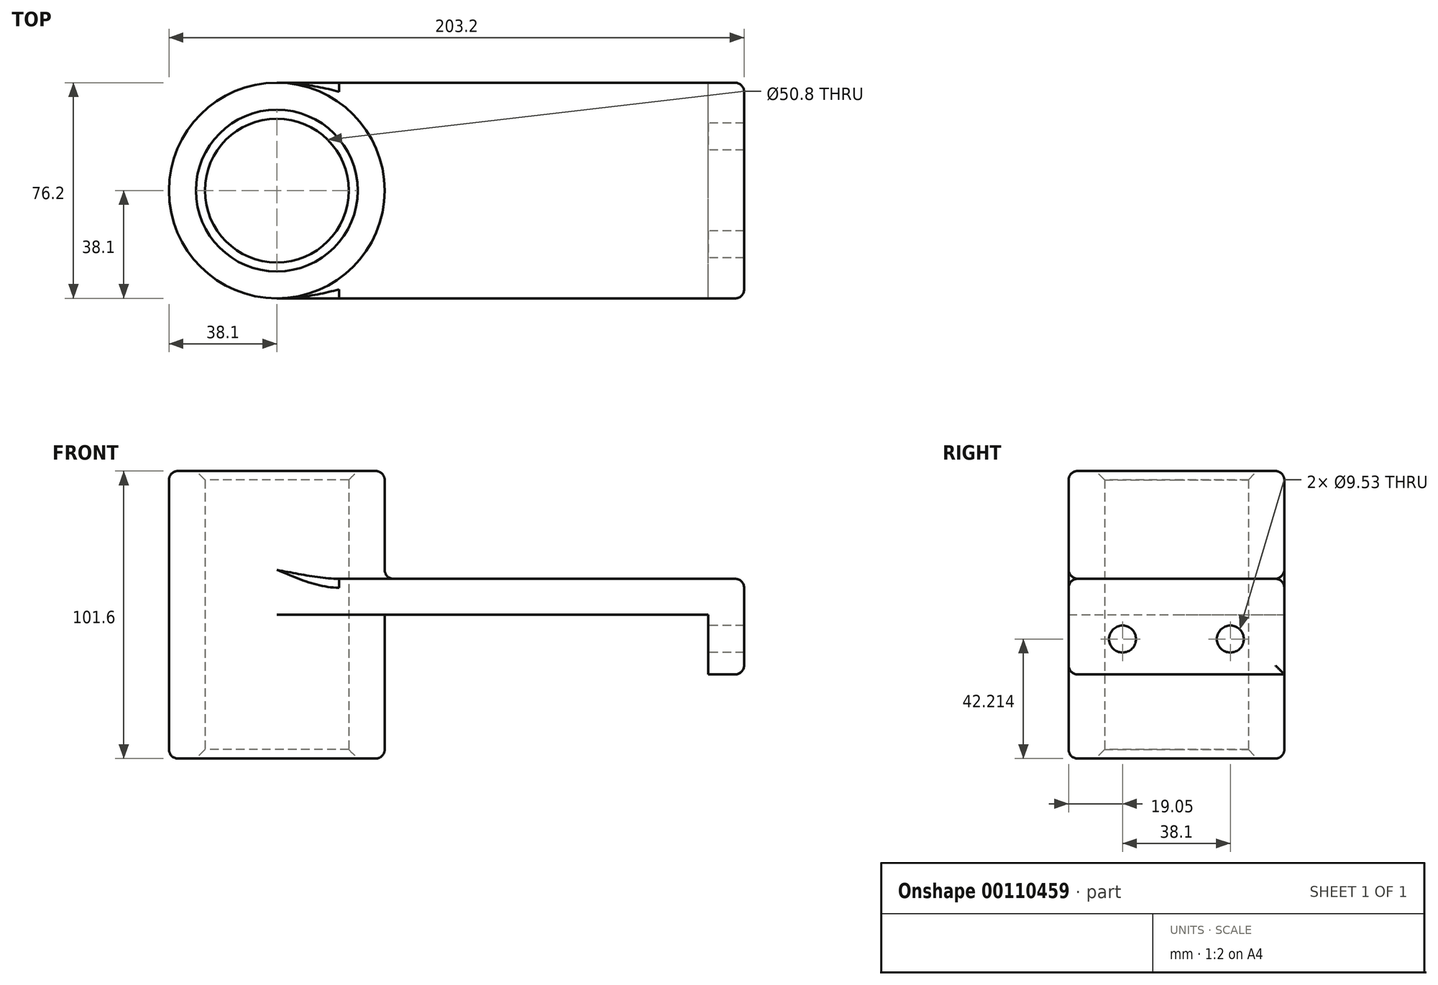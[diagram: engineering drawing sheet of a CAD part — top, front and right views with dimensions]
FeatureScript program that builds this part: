
annotation { "Feature Type Name" : "Feature", "Feature Type Description" : "" }
export const myFeature = defineFeature(function(context is Context, id is Id, definition is map)
    precondition{}
    {
        {
            var Q0;
            Q0=qCreatedBy(makeId("Top.planeOp"),FACE);
            var sketch = newSketch(context, id + "F0", { "sketchPlane" : qUnion([Q0])});
            skLineSegment(sketch, "E0.bottom", {"start": v(76.2, -38.1) * mm, "end": v(-76.2, -38.1) * mm});
            skLineSegment(sketch, "E0.top", {"start": v(76.2, 38.1) * mm, "end": v(-76.2, 38.1) * mm});
            skLineSegment(sketch, "E0.left", {"start": v(76.2, -38.1) * mm, "end": v(76.2, 38.1) * mm});
            skLineSegment(sketch, "E0.right", {"start": v(-76.2, -38.1) * mm, "end": v(-76.2, 38.1) * mm});
            skPoint(sketch, "E0.middle", {"position": v(0, 0) * mm});
            skCircle(sketch, "E1", {"center": v(-76.2, 0) * mm, "radius": 38.1 * mm});
            skCircle(sketch, "E2", {"center": v(-76.2, 0) * mm, "radius": 25.4 * mm});
            skSolve(sketch);
        }
        {
            var Q0;
            Q0 = qSketchRegion(id + "F0", true);
            extrude(context, id + "F1", {"entities" : qUnion([Q0]), "depth" : 12.7 * mm});
        }
        {
            var Q0;
            {var subQ1=sQuery(id+"F0.wireOp",EDGE,"E0.right");var subQ3=sQuery(id+"F0.wireOp",EDGE,"E2");var subQ4=makeQuery(id+"F0.imprint","INTERSECT",VERTEX,{"disambiguationData":[OD(0.0)],"derivedFrom":[subQ1,subQ3]});Q0=makeQuery(id+"F0.imprint","IMPRINT",FACE,{"disambiguationData":[TD([[makeQuery(id+"F0.imprint","IMPRINT",EDGE,{"disambiguationData":[TD([[subQ4,1.0]])],"derivedFrom":subQ3}),-1.0]])]});}
            var Q1;
            {var subQ1=sQuery(id+"F0.wireOp",EDGE,"E0.right");var subQ3=sQuery(id+"F0.wireOp",EDGE,"E2");var subQ4=makeQuery(id+"F0.imprint","INTERSECT",VERTEX,{"disambiguationData":[OD(0.0)],"derivedFrom":[subQ1,subQ3]});Q1=makeQuery(id+"F0.imprint","IMPRINT",FACE,{"disambiguationData":[TD([[makeQuery(id+"F0.imprint","IMPRINT",EDGE,{"disambiguationData":[TD([[subQ4,-1.0]])],"derivedFrom":subQ3}),-1.0]])]});}
            extrude(context, id + "F2", {"entities" : qUnion([Q0, Q1]), "operationType" : NewBodyOperationType.ADD, "depth" : 50.8 * mm, "hasSecondDirection" : true, "secondDirectionOppositeDirection" : true, "secondDirectionDepth" : 50.8 * mm});
        }
        {
            var Q0;
            Q0=makeQuery(id+"F1.opExtrude","SWEPT_FACE",FACE,{"disambiguationData":[OSD([sQuery(id+"F0.wireOp",EDGE,"E0.left")])]});
            var sketch = newSketch(context, id + "F3", { "sketchPlane" : qUnion([Q0])});
            skLineSegment(sketch, "E3.bottom", {"start": v(-38.1, 12.7) * mm, "end": v(38.1, 12.7) * mm});
            skLineSegment(sketch, "E3.top", {"start": v(-38.1, -21.07) * mm, "end": v(38.1, -21.07) * mm});
            skLineSegment(sketch, "E3.left", {"start": v(-38.1, 12.7) * mm, "end": v(-38.1, -21.07) * mm});
            skLineSegment(sketch, "E3.right", {"start": v(38.1, 12.7) * mm, "end": v(38.1, -21.07) * mm});
            skCircle(sketch, "E4", {"center": v(-19.05, -8.59) * mm, "radius": 4.76 * mm});
            skLineSegment(sketch, "E5", {"start": v(0, 0) * mm, "end": v(0, -21.07) * mm, "construction": true});
            skCircle(sketch, "E6.MirrorC", {"center": v(19.05, -8.59) * mm, "radius": 4.76 * mm});
            skSolve(sketch);
        }
        {
            var Q0;
            Q0 = qSketchRegion(id + "F3", true);
            extrude(context, id + "F4", {"entities" : qUnion([Q0]), "operationType" : NewBodyOperationType.ADD, "depth" : 12.7 * mm});
        }
        {
            var Q0;
            {var subQ0=sQuery(id+"F0.wireOp",EDGE,"E1");Q0=makeQuery(id+"F2.boolean.opBoolean","INTERSECT",EDGE,{"derivedFrom":[makeQuery(id+"F1.opExtrude","CAP_FACE",FACE,{"disambiguationData":[OSD([sQuery(id+"F0.wireOp",EDGE,"E0.bottom"),sQuery(id+"F0.wireOp",EDGE,"E0.top"),sQuery(id+"F0.wireOp",EDGE,"E0.left"),subQ0,sQuery(id+"F0.wireOp",EDGE,"E2")])],"isStart":false}),makeQuery(id+"F2.opExtrude","SWEPT_FACE",FACE,{"disambiguationData":[OSD([subQ0])]})]});}
            fillet(context, id + "F5", {"entities" : qUnion([Q0]), "radius" : 3.17 * mm, "tangentPropagation" : true, "allowEdgeOverflow" : false});
        }
        {
            var Q0;
            Q0=makeQuery(id+"F4.opExtrude","CAP_EDGE",EDGE,{"disambiguationData":[OSD([sQuery(id+"F3.wireOp",EDGE,"E3.bottom")])],"isStart":false});
            fillet(context, id + "F6", {"entities" : qUnion([Q0]), "radius" : 3.17 * mm, "tangentPropagation" : true, "allowEdgeOverflow" : false});
        }
        {
            var Q0;
            Q0=makeQuery(id+"F2.opExtrude","CAP_EDGE",EDGE,{"disambiguationData":[OSD([sQuery(id+"F0.wireOp",EDGE,"E1")])],"isStart":false});
            fillet(context, id + "F7", {"entities" : qUnion([Q0]), "radius" : 3.17 * mm, "tangentPropagation" : true, "allowEdgeOverflow" : false});
        }
        {
            var Q0;
            Q0=makeQuery(id+"F4.boolean.opBoolean","MERGE",EDGE,{"derivedFrom":[makeQuery(id+"F1.opExtrude","CAP_EDGE",EDGE,{"disambiguationData":[OSD([sQuery(id+"F0.wireOp",EDGE,"E0.bottom")])],"isStart":false}),makeQuery(id+"F4.opExtrude","SWEPT_EDGE",EDGE,{"disambiguationData":[OSD([sQuery(id+"F3.wireOp",EDGE,"E3.bottom"),sQuery(id+"F3.wireOp",EDGE,"E3.left")])]})]});
            fillet(context, id + "F8", {"entities" : qUnion([Q0]), "radius" : 3.17 * mm, "tangentPropagation" : true, "allowEdgeOverflow" : false});
        }
        {
            var Q0;
            {var subQ0=sQuery(id+"F0.wireOp",EDGE,"E2");Q0=makeQuery(id+"F2.boolean.opBoolean","MERGE",FACE,{"derivedFrom":[makeQuery(id+"F1.opExtrude","SWEPT_FACE",FACE,{"disambiguationData":[OSD([subQ0])]}),makeQuery(id+"F2.opExtrude","SWEPT_FACE",FACE,{"disambiguationData":[OSD([subQ0])]})]});}
            chamfer(context, id + "F9", {"entities" : qUnion([Q0]), "width" : 3.17 * mm, "tangentPropagation" : true});
        }
        {
            var Q0;
            Q0=makeQuery(id+"F2.opExtrude","CAP_EDGE",EDGE,{"disambiguationData":[OSD([sQuery(id+"F0.wireOp",EDGE,"E1")])],"isStart":true});
            fillet(context, id + "F10", {"entities" : qUnion([Q0]), "radius" : 3.17 * mm, "tangentPropagation" : true, "allowEdgeOverflow" : false});
        }
        {
            var Q0;
            Q0=makeQuery(id+"F4.boolean.opBoolean","MERGE",EDGE,{"derivedFrom":[makeQuery(id+"F1.opExtrude","CAP_EDGE",EDGE,{"disambiguationData":[OSD([sQuery(id+"F0.wireOp",EDGE,"E0.top")])],"isStart":false}),makeQuery(id+"F4.opExtrude","SWEPT_EDGE",EDGE,{"disambiguationData":[OSD([sQuery(id+"F3.wireOp",EDGE,"E3.bottom"),sQuery(id+"F3.wireOp",EDGE,"E3.right")])]})]});
            var Q1;
            Q1=makeQuery(id+"F4.opExtrude","CAP_EDGE",EDGE,{"disambiguationData":[OSD([sQuery(id+"F3.wireOp",EDGE,"E3.top")])],"isStart":false});
            fillet(context, id + "F11", {"entities" : qUnion([Q0, Q1]), "radius" : 3.17 * mm, "tangentPropagation" : true, "allowEdgeOverflow" : false});
        }
    });
